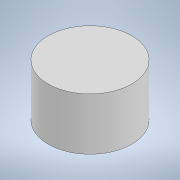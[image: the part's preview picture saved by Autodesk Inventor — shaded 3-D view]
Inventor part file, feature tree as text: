
AUTODESK INVENTOR PART (.ipt)
format: ipt  version: 2022 (Build 260153000, 153)  size: 88,064 bytes
history: native  units: mm
features: extrude x1, sketch x1
ambient origin geometry x8: Origin, YZ Plane, XZ Plane, XY Plane, X Axis, Y Axis, Z Axis, Center Point
bodies: Solid1 (feature_tree)
feature tree (2):
  extrude  "Extrusion1"  Depth=5.0mm TaperAngle=0.0deg
  sketch  "Sketch1"  dims[d0=8.0mm d1=5.0mm d2=0.0mm]
